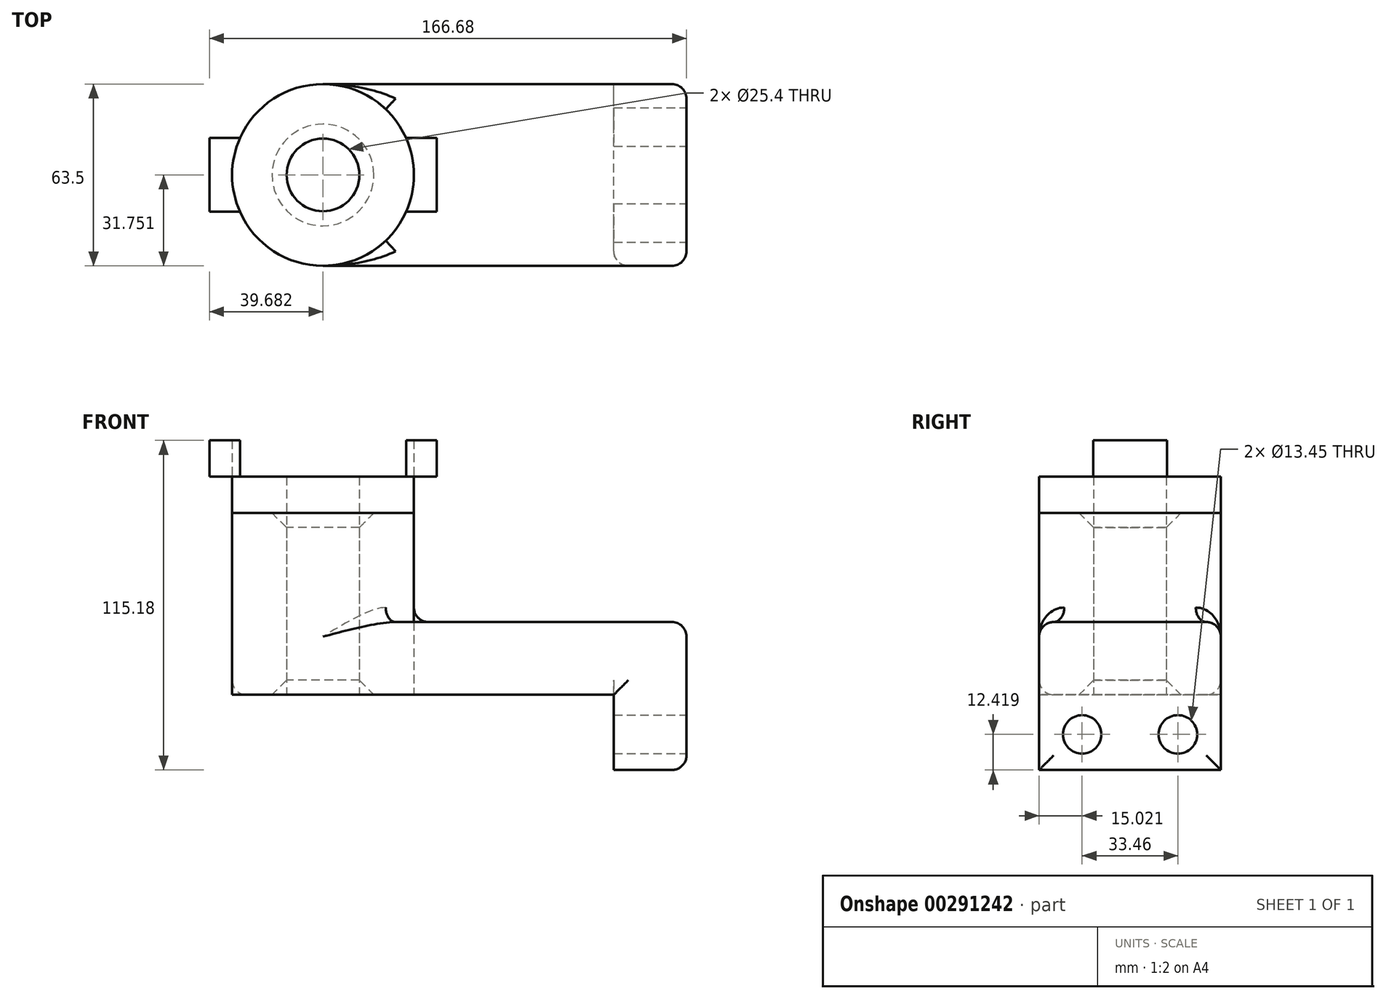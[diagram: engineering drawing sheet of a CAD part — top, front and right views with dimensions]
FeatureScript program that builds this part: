
annotation { "Feature Type Name" : "Feature", "Feature Type Description" : "" }
export const myFeature = defineFeature(function(context is Context, id is Id, definition is map)
    precondition{}
    {
        {
            var Q0;
            Q0=qCreatedBy(makeId("Top.planeOp"),FACE);
            var sketch = newSketch(context, id + "F0", { "sketchPlane" : qUnion([Q0])});
            skLineSegment(sketch, "E0.bottom", {"start": v(-29.4, -9.26) * mm, "end": v(97.6, -9.26) * mm});
            skLineSegment(sketch, "E0.top", {"start": v(-29.4, 54.24) * mm, "end": v(97.6, 54.24) * mm});
            skLineSegment(sketch, "E0.left", {"start": v(-29.4, -9.26) * mm, "end": v(-29.4, 54.24) * mm});
            skLineSegment(sketch, "E0.right", {"start": v(97.6, -9.26) * mm, "end": v(97.6, 54.24) * mm});
            skCircle(sketch, "E1", {"center": v(-29.4, 22.5) * mm, "radius": 31.75 * mm});
            skCircle(sketch, "E2", {"center": v(-29.4, 22.5) * mm, "radius": 12.7 * mm});
            skSolve(sketch);
        }
        {
            var Q0;
            {var subQ0=sQuery(id+"F0.wireOp",EDGE,"E0.bottom");Q0=makeQuery(id+"F0.imprint","IMPRINT",FACE,{"disambiguationData":[TD([[makeQuery(id+"F0.imprint","IMPRINT",EDGE,{"derivedFrom":subQ0}),1.0]])]});}
            var Q1;
            {var subQ1=sQuery(id+"F0.wireOp",EDGE,"E0.left");var subQ3=sQuery(id+"F0.wireOp",EDGE,"E2");var subQ4=makeQuery(id+"F0.imprint","INTERSECT",VERTEX,{"disambiguationData":[OD(0.0)],"derivedFrom":[subQ1,subQ3]});Q1=makeQuery(id+"F0.imprint","IMPRINT",FACE,{"disambiguationData":[TD([[makeQuery(id+"F0.imprint","IMPRINT",EDGE,{"disambiguationData":[TD([[subQ4,-1.0]])],"derivedFrom":subQ3}),-1.0]])]});}
            var Q2;
            {var subQ1=sQuery(id+"F0.wireOp",EDGE,"E0.left");var subQ3=sQuery(id+"F0.wireOp",EDGE,"E2");var subQ4=makeQuery(id+"F0.imprint","INTERSECT",VERTEX,{"disambiguationData":[OD(0.0)],"derivedFrom":[subQ1,subQ3]});Q2=makeQuery(id+"F0.imprint","IMPRINT",FACE,{"disambiguationData":[TD([[makeQuery(id+"F0.imprint","IMPRINT",EDGE,{"disambiguationData":[TD([[subQ4,1.0]])],"derivedFrom":subQ3}),-1.0]])]});}
            extrude(context, id + "F1", {"entities" : qUnion([Q0, Q1, Q2]), "depth" : 25.4 * mm});
        }
        {
            var Q0;
            {var subQ1=sQuery(id+"F0.wireOp",EDGE,"E0.left");var subQ3=sQuery(id+"F0.wireOp",EDGE,"E2");var subQ4=makeQuery(id+"F0.imprint","INTERSECT",VERTEX,{"disambiguationData":[OD(0.0)],"derivedFrom":[subQ1,subQ3]});Q0=makeQuery(id+"F0.imprint","IMPRINT",FACE,{"disambiguationData":[TD([[makeQuery(id+"F0.imprint","IMPRINT",EDGE,{"disambiguationData":[TD([[subQ4,1.0]])],"derivedFrom":subQ3}),-1.0]])]});}
            var Q1;
            {var subQ1=sQuery(id+"F0.wireOp",EDGE,"E0.left");var subQ3=sQuery(id+"F0.wireOp",EDGE,"E2");var subQ4=makeQuery(id+"F0.imprint","INTERSECT",VERTEX,{"disambiguationData":[OD(0.0)],"derivedFrom":[subQ1,subQ3]});Q1=makeQuery(id+"F0.imprint","IMPRINT",FACE,{"disambiguationData":[TD([[makeQuery(id+"F0.imprint","IMPRINT",EDGE,{"disambiguationData":[TD([[subQ4,-1.0]])],"derivedFrom":subQ3}),-1.0]])]});}
            extrude(context, id + "F2", {"entities" : qUnion([Q0, Q1]), "operationType" : NewBodyOperationType.ADD, "depth" : 63.5 * mm});
        }
        {
            var Q0;
            Q0=makeQuery(id+"F1.opExtrude","SWEPT_FACE",FACE,{"disambiguationData":[OSD([sQuery(id+"F0.wireOp",EDGE,"E0.right")])]});
            var sketch = newSketch(context, id + "F3", { "sketchPlane" : qUnion([Q0])});
            skLineSegment(sketch, "E3.bottom", {"start": v(-9.26, 25.4) * mm, "end": v(54.24, 25.4) * mm});
            skLineSegment(sketch, "E3.top", {"start": v(-9.26, -26.28) * mm, "end": v(54.24, -26.28) * mm});
            skLineSegment(sketch, "E3.left", {"start": v(-9.26, 25.4) * mm, "end": v(-9.26, -26.28) * mm});
            skLineSegment(sketch, "E3.right", {"start": v(54.24, 25.4) * mm, "end": v(54.24, -26.28) * mm});
            skLineSegment(sketch, "E4", {"start": v(22.5, 0) * mm, "end": v(22.5, -26.28) * mm, "construction": true});
            skCircle(sketch, "E5", {"center": v(5.76, -13.86) * mm, "radius": 6.73 * mm});
            skCircle(sketch, "E6.MirrorC", {"center": v(39.22, -13.86) * mm, "radius": 6.73 * mm});
            skSolve(sketch);
        }
        {
            var Q0;
            Q0 = qSketchRegion(id + "F3", true);
            extrude(context, id + "F4", {"entities" : qUnion([Q0]), "operationType" : NewBodyOperationType.ADD, "oppositeDirection" : true, "depth" : 25.4 * mm});
        }
        {
            var Q0;
            Q0=makeQuery(id+"F1.opExtrude","CAP_FACE",FACE,{"disambiguationData":[OSD([sQuery(id+"F0.wireOp",EDGE,"E0.bottom"),sQuery(id+"F0.wireOp",EDGE,"E0.top"),sQuery(id+"F0.wireOp",EDGE,"E0.right"),sQuery(id+"F0.wireOp",EDGE,"E1"),sQuery(id+"F0.wireOp",EDGE,"E2")])],"isStart":false});
            var Q1;
            Q1=makeQuery(id+"F1.opExtrude","CAP_EDGE",EDGE,{"disambiguationData":[OSD([sQuery(id+"F0.wireOp",EDGE,"E0.bottom")])],"isStart":true});
            var Q2;
            Q2=makeQuery(id+"F4.opExtrude","CAP_EDGE",EDGE,{"disambiguationData":[OSD([sQuery(id+"F3.wireOp",EDGE,"E3.left")])],"isStart":false});
            var Q3;
            Q3=makeQuery(id+"F4.boolean.opBoolean","MERGE",EDGE,{"derivedFrom":[makeQuery(id+"F1.opExtrude","SWEPT_EDGE",EDGE,{"disambiguationData":[OSD([sQuery(id+"F0.wireOp",EDGE,"E0.bottom"),sQuery(id+"F0.wireOp",EDGE,"E0.right")])]}),makeQuery(id+"F4.opExtrude","CAP_EDGE",EDGE,{"disambiguationData":[OSD([sQuery(id+"F3.wireOp",EDGE,"E3.left")])],"isStart":true})]});
            var Q4;
            Q4=makeQuery(id+"F4.boolean.opBoolean","MERGE",EDGE,{"derivedFrom":[makeQuery(id+"F1.opExtrude","SWEPT_EDGE",EDGE,{"disambiguationData":[OSD([sQuery(id+"F0.wireOp",EDGE,"E0.top"),sQuery(id+"F0.wireOp",EDGE,"E0.right")])]}),makeQuery(id+"F4.opExtrude","CAP_EDGE",EDGE,{"disambiguationData":[OSD([sQuery(id+"F3.wireOp",EDGE,"E3.right")])],"isStart":true})]});
            var Q5;
            Q5=makeQuery(id+"F4.opExtrude","CAP_EDGE",EDGE,{"disambiguationData":[OSD([sQuery(id+"F3.wireOp",EDGE,"E3.top")])],"isStart":true});
            fillet(context, id + "F5", {"entities" : qUnion([Q0, Q1, Q2, Q3, Q4, Q5]), "radius" : 5.08 * mm, "tangentPropagation" : true, "allowEdgeOverflow" : false});
        }
        {
            var Q0;
            {var subQ0=sQuery(id+"F0.wireOp",EDGE,"E2");Q0=makeQuery(id+"F2.boolean.opBoolean","MERGE",FACE,{"derivedFrom":[makeQuery(id+"F1.opExtrude","SWEPT_FACE",FACE,{"disambiguationData":[OSD([subQ0])]}),makeQuery(id+"F2.opExtrude","SWEPT_FACE",FACE,{"disambiguationData":[OSD([subQ0])]})]});}
            chamfer(context, id + "F6", {"entities" : qUnion([Q0]), "width" : 5.08 * mm, "tangentPropagation" : true});
        }
        {
            var Q0;
            {var subQ0=sQuery(id+"F0.wireOp",EDGE,"E2");var subQ1=sQuery(id+"F0.wireOp",EDGE,"E0.left");var subQ2=makeQuery(id+"F0.imprint","INTERSECT",VERTEX,{"disambiguationData":[OD(0.0)],"derivedFrom":[subQ1,subQ0]});Q0=makeQuery(id+"F0.imprint","IMPRINT",FACE,{"disambiguationData":[TD([[makeQuery(id+"F0.imprint","IMPRINT",EDGE,{"disambiguationData":[TD([[subQ2,-1.0]])],"derivedFrom":subQ1}),1.0]])]});}
            var Q1;
            {var subQ0=sQuery(id+"F0.wireOp",EDGE,"E2");var subQ1=sQuery(id+"F0.wireOp",EDGE,"E0.left");var subQ2=makeQuery(id+"F0.imprint","INTERSECT",VERTEX,{"disambiguationData":[OD(0.0)],"derivedFrom":[subQ1,subQ0]});Q1=makeQuery(id+"F0.imprint","IMPRINT",FACE,{"disambiguationData":[TD([[makeQuery(id+"F0.imprint","IMPRINT",EDGE,{"disambiguationData":[TD([[subQ2,-1.0]])],"derivedFrom":subQ1}),-1.0]])]});}
            extrude(context, id + "F7", {"entities" : qUnion([Q0, Q1]), "depth" : 76.2 * mm});
        }
        {
            var Q0;
            Q0=makeQuery(id+"F7.opExtrude","CAP_FACE",FACE,{"disambiguationData":[OSD([sQuery(id+"F0.wireOp",EDGE,"E2")])],"isStart":false});
            var sketch = newSketch(context, id + "F8", { "sketchPlane" : qUnion([Q0])});
            skLineSegment(sketch, "E7.bottom", {"start": v(10.28, 35.39) * mm, "end": v(-69.1, 35.39) * mm});
            skLineSegment(sketch, "E7.top", {"start": v(10.28, 9.6) * mm, "end": v(-69.1, 9.6) * mm});
            skLineSegment(sketch, "E7.left", {"start": v(10.28, 35.39) * mm, "end": v(10.28, 9.6) * mm});
            skLineSegment(sketch, "E7.right", {"start": v(-69.1, 35.39) * mm, "end": v(-69.1, 9.6) * mm});
            skPoint(sketch, "E7.middle", {"position": v(-29.4, 22.5) * mm});
            skSolve(sketch);
        }
        {
            var Q0;
            Q0=makeQuery(id+"F8.imprint","IMPRINT",FACE,{"disambiguationData":[TD([[makeQuery(id+"F8.imprint","IMPRINT",EDGE,{"derivedFrom":sQuery(id+"F8.wireOp",EDGE,"E7.bottom")}),1.0]])]});
            extrude(context, id + "F9", {"entities" : qUnion([Q0]), "depth" : 12.7 * mm});
        }
    });
